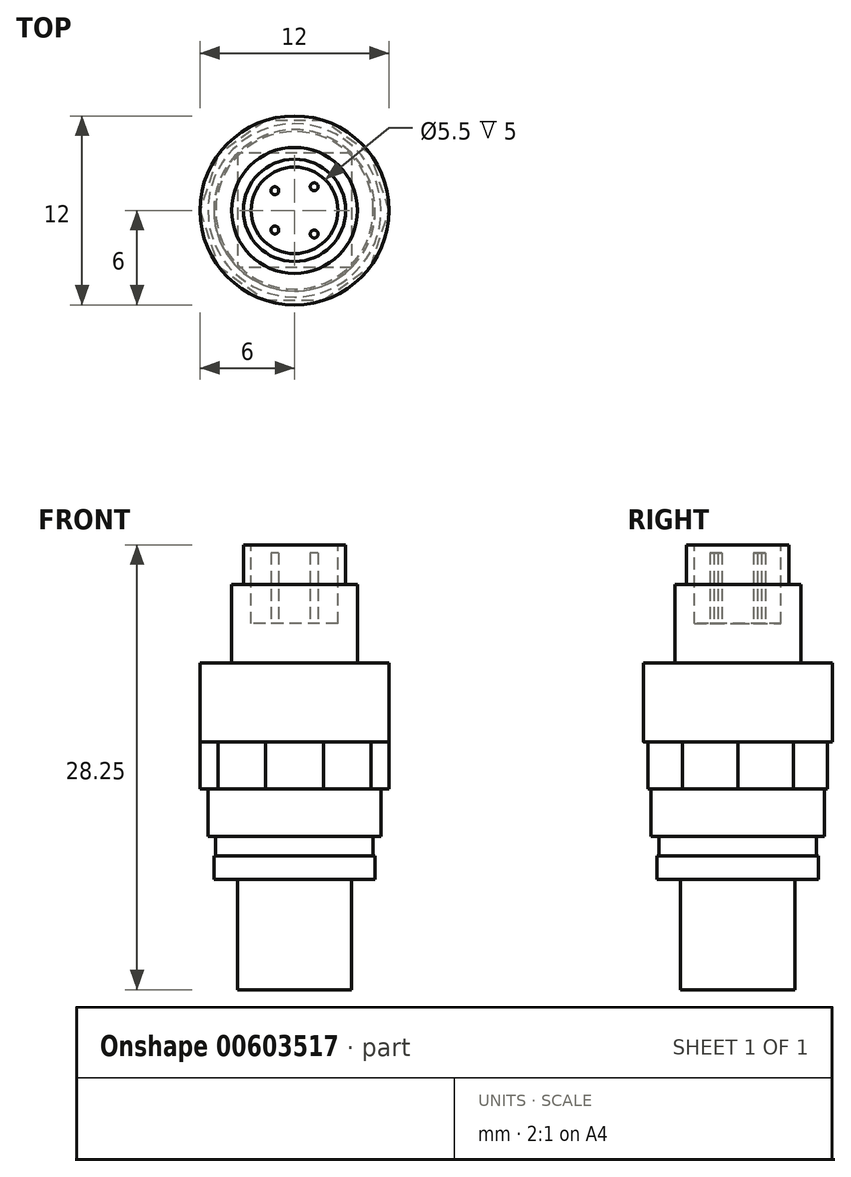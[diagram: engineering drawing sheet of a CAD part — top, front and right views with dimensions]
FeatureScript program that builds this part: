
annotation { "Feature Type Name" : "Feature", "Feature Type Description" : "" }
export const myFeature = defineFeature(function(context is Context, id is Id, definition is map)
    precondition{}
    {
        {
            var Q0;
            Q0=qCreatedBy(makeId("Top.planeOp"),FACE);
            var sketch = newSketch(context, id + "F0", { "sketchPlane" : qUnion([Q0])});
            skCircle(sketch, "E0", {"center": v(0, 0) * mm, "radius": 3.25 * mm});
            skSolve(sketch);
        }
        {
            var Q0;
            Q0=makeQuery(id+"F0.imprint","IMPRINT",FACE,{"disambiguationData":[TD([[makeQuery(id+"F0.imprint","IMPRINT",EDGE,{"derivedFrom":sQuery(id+"F0.wireOp",EDGE,"E0")}),1.0]])]});
            extrude(context, id + "F1", {"entities" : qUnion([Q0]), "oppositeDirection" : true, "depth" : 2.5 * mm, "offsetDistance" : 25 * mm});
        }
        {
            var Q0;
            Q0=makeQuery(id+"F1.opExtrude","CAP_FACE",FACE,{"disambiguationData":[OSD([sQuery(id+"F0.wireOp",EDGE,"E0")])],"isStart":false});
            var sketch = newSketch(context, id + "F2", { "sketchPlane" : qUnion([Q0])});
            skCircle(sketch, "E1", {"center": v(0, 0) * mm, "radius": 4 * mm});
            skSolve(sketch);
        }
        {
            var Q0;
            Q0=makeQuery(id+"F2.imprint","IMPRINT",FACE,{"disambiguationData":[TD([[makeQuery(id+"F2.imprint","IMPRINT",EDGE,{"derivedFrom":makeQuery(id+"F1.opExtrude","CAP_EDGE",EDGE,{"disambiguationData":[OSD([sQuery(id+"F0.wireOp",EDGE,"E0")])],"isStart":false})}),-1.0]])]});
            var Q1;
            Q1=makeQuery(id+"F2.imprint","IMPRINT",FACE,{"disambiguationData":[TD([[makeQuery(id+"F2.imprint","IMPRINT",EDGE,{"derivedFrom":sQuery(id+"F2.wireOp",EDGE,"E1")}),1.0]])]});
            extrude(context, id + "F3", {"entities" : qUnion([Q0, Q1]), "operationType" : NewBodyOperationType.ADD, "depth" : 5 * mm, "offsetDistance" : 25 * mm});
        }
        {
            var Q0;
            Q0=makeQuery(id+"F3.opExtrude","CAP_FACE",FACE,{"disambiguationData":[OSD([sQuery(id+"F2.wireOp",EDGE,"E1")])],"isStart":false});
            var sketch = newSketch(context, id + "F4", { "sketchPlane" : qUnion([Q0])});
            skCircle(sketch, "E2", {"center": v(0, 0) * mm, "radius": 6 * mm});
            skSolve(sketch);
        }
        {
            var Q0;
            Q0=makeQuery(id+"F4.imprint","IMPRINT",FACE,{"disambiguationData":[TD([[makeQuery(id+"F4.imprint","IMPRINT",EDGE,{"derivedFrom":sQuery(id+"F4.wireOp",EDGE,"E2")}),1.0]])]});
            var Q1;
            Q1=makeQuery(id+"F4.imprint","IMPRINT",FACE,{"disambiguationData":[TD([[makeQuery(id+"F4.imprint","IMPRINT",EDGE,{"derivedFrom":makeQuery(id+"F3.opExtrude","CAP_EDGE",EDGE,{"disambiguationData":[OSD([sQuery(id+"F2.wireOp",EDGE,"E1")])],"isStart":false})}),1.0]])]});
            extrude(context, id + "F5", {"entities" : qUnion([Q0, Q1]), "operationType" : NewBodyOperationType.ADD, "depth" : 5 * mm, "offsetDistance" : 25 * mm});
        }
        {
            var Q0;
            Q0=makeQuery(id+"F5.opExtrude","CAP_FACE",FACE,{"disambiguationData":[OSD([sQuery(id+"F4.wireOp",EDGE,"E2")])],"isStart":false});
            var sketch = newSketch(context, id + "F6", { "sketchPlane" : qUnion([Q0])});
            skCircle(sketch, "E3.cCircle", {"center": v(0, 0) * mm, "radius": 6 * mm, "construction": true});
            skLineSegment(sketch, "E3.0", {"start": v(6, 0) * mm, "end": v(4.85, -3.53) * mm});
            skLineSegment(sketch, "E3.1", {"start": v(4.85, -3.53) * mm, "end": v(1.85, -5.7) * mm});
            skLineSegment(sketch, "E3.2", {"start": v(1.85, -5.7) * mm, "end": v(-1.85, -5.7) * mm});
            skLineSegment(sketch, "E3.3", {"start": v(-1.85, -5.7) * mm, "end": v(-4.85, -3.53) * mm});
            skLineSegment(sketch, "E3.4", {"start": v(-4.85, -3.53) * mm, "end": v(-6, 0) * mm});
            skLineSegment(sketch, "E3.5", {"start": v(-6, 0) * mm, "end": v(-4.85, 3.53) * mm});
            skLineSegment(sketch, "E3.6", {"start": v(-4.85, 3.53) * mm, "end": v(-1.85, 5.7) * mm});
            skLineSegment(sketch, "E3.7", {"start": v(-1.85, 5.7) * mm, "end": v(1.85, 5.7) * mm});
            skLineSegment(sketch, "E3.8", {"start": v(1.85, 5.7) * mm, "end": v(4.85, 3.53) * mm});
            skLineSegment(sketch, "E3.9", {"start": v(4.85, 3.53) * mm, "end": v(6, 0) * mm});
            skSolve(sketch);
        }
        {
            var Q0;
            Q0=makeQuery(id+"F6.imprint","IMPRINT",FACE,{"disambiguationData":[TD([[makeQuery(id+"F6.imprint","IMPRINT",EDGE,{"derivedFrom":sQuery(id+"F6.wireOp",EDGE,"E3.0")}),-1.0]])]});
            extrude(context, id + "F7", {"entities" : qUnion([Q0]), "operationType" : NewBodyOperationType.ADD, "depth" : 3 * mm, "offsetDistance" : 25 * mm});
        }
        {
            var Q0;
            Q0=makeQuery(id+"F7.opExtrude","CAP_FACE",FACE,{"disambiguationData":[OSD([sQuery(id+"F6.wireOp",EDGE,"E3.0"),sQuery(id+"F6.wireOp",EDGE,"E3.1"),sQuery(id+"F6.wireOp",EDGE,"E3.2"),sQuery(id+"F6.wireOp",EDGE,"E3.3"),sQuery(id+"F6.wireOp",EDGE,"E3.4"),sQuery(id+"F6.wireOp",EDGE,"E3.5"),sQuery(id+"F6.wireOp",EDGE,"E3.6"),sQuery(id+"F6.wireOp",EDGE,"E3.7"),sQuery(id+"F6.wireOp",EDGE,"E3.8"),sQuery(id+"F6.wireOp",EDGE,"E3.9")])],"isStart":false});
            var sketch = newSketch(context, id + "F8", { "sketchPlane" : qUnion([Q0])});
            skCircle(sketch, "E4", {"center": v(0, 0) * mm, "radius": 5.5 * mm});
            skSolve(sketch);
        }
        {
            var Q0;
            Q0=makeQuery(id+"F8.imprint","IMPRINT",FACE,{"disambiguationData":[TD([[makeQuery(id+"F8.imprint","IMPRINT",EDGE,{"derivedFrom":sQuery(id+"F8.wireOp",EDGE,"E4")}),1.0]])]});
            extrude(context, id + "F9", {"entities" : qUnion([Q0]), "operationType" : NewBodyOperationType.ADD, "depth" : 3 * mm, "offsetDistance" : 25 * mm});
        }
        {
            var Q0;
            Q0=makeQuery(id+"F9.opExtrude","CAP_FACE",FACE,{"disambiguationData":[OSD([sQuery(id+"F8.wireOp",EDGE,"E4")])],"isStart":false});
            var sketch = newSketch(context, id + "F10", { "sketchPlane" : qUnion([Q0])});
            skCircle(sketch, "E5", {"center": v(0, 0) * mm, "radius": 5 * mm});
            skSolve(sketch);
        }
        {
            var Q0;
            Q0=makeQuery(id+"F10.imprint","IMPRINT",FACE,{"disambiguationData":[TD([[makeQuery(id+"F10.imprint","IMPRINT",EDGE,{"derivedFrom":sQuery(id+"F10.wireOp",EDGE,"E5")}),1.0]])]});
            extrude(context, id + "F11", {"entities" : qUnion([Q0]), "operationType" : NewBodyOperationType.ADD, "depth" : 1.25 * mm, "offsetDistance" : 25 * mm});
        }
        {
            var Q0;
            Q0=makeQuery(id+"F11.opExtrude","CAP_FACE",FACE,{"disambiguationData":[OSD([sQuery(id+"F10.wireOp",EDGE,"E5")])],"isStart":false});
            var sketch = newSketch(context, id + "F12", { "sketchPlane" : qUnion([Q0])});
            skCircle(sketch, "E6", {"center": v(0, 0) * mm, "radius": 5.13 * mm});
            skSolve(sketch);
        }
        {
            var Q0;
            Q0=makeQuery(id+"F12.imprint","IMPRINT",FACE,{"disambiguationData":[TD([[makeQuery(id+"F12.imprint","IMPRINT",EDGE,{"derivedFrom":sQuery(id+"F12.wireOp",EDGE,"E6")}),1.0]])]});
            var Q1;
            Q1=makeQuery(id+"F12.imprint","IMPRINT",FACE,{"disambiguationData":[TD([[makeQuery(id+"F12.imprint","IMPRINT",EDGE,{"derivedFrom":makeQuery(id+"F11.opExtrude","CAP_EDGE",EDGE,{"disambiguationData":[OSD([sQuery(id+"F10.wireOp",EDGE,"E5")])],"isStart":false})}),1.0]])]});
            extrude(context, id + "F13", {"entities" : qUnion([Q0, Q1]), "operationType" : NewBodyOperationType.ADD, "depth" : 1.5 * mm, "offsetDistance" : 25 * mm});
        }
        {
            var Q0;
            Q0=makeQuery(id+"F13.opExtrude","CAP_FACE",FACE,{"disambiguationData":[OSD([sQuery(id+"F12.wireOp",EDGE,"E6")])],"isStart":false});
            var sketch = newSketch(context, id + "F14", { "sketchPlane" : qUnion([Q0])});
            skLineSegment(sketch, "E7.bottom", {"start": v(3.62, -3.62) * mm, "end": v(-3.62, -3.62) * mm});
            skLineSegment(sketch, "E7.top", {"start": v(3.62, 3.62) * mm, "end": v(-3.62, 3.62) * mm});
            skLineSegment(sketch, "E7.left", {"start": v(3.62, -3.62) * mm, "end": v(3.62, 3.62) * mm});
            skLineSegment(sketch, "E7.right", {"start": v(-3.62, -3.62) * mm, "end": v(-3.62, 3.62) * mm});
            skPoint(sketch, "E7.middle", {"position": v(0, 0) * mm});
            skSolve(sketch);
        }
        {
            var Q0;
            Q0=makeQuery(id+"F14.imprint","IMPRINT",FACE,{"disambiguationData":[TD([[makeQuery(id+"F14.imprint","IMPRINT",EDGE,{"derivedFrom":sQuery(id+"F14.wireOp",EDGE,"E7.bottom")}),-1.0]])]});
            extrude(context, id + "F15", {"entities" : qUnion([Q0]), "operationType" : NewBodyOperationType.ADD, "depth" : 7 * mm, "offsetDistance" : 25 * mm});
        }
        {
            var Q0;
            Q0=makeQuery(id+"F1.opExtrude","CAP_FACE",FACE,{"disambiguationData":[OSD([sQuery(id+"F0.wireOp",EDGE,"E0")])],"isStart":true});
            var sketch = newSketch(context, id + "F16", { "sketchPlane" : qUnion([Q0])});
            skCircle(sketch, "E8.0", {"center": v(0, 0) * mm, "radius": 3.25 * mm, "construction": true});
            skCircle(sketch, "E9.0", {"center": v(0, 0) * mm, "radius": 2.75 * mm});
            skSolve(sketch);
        }
        {
            var Q0;
            Q0=makeQuery(id+"F16.imprint","IMPRINT",FACE,{"disambiguationData":[TD([[makeQuery(id+"F16.imprint","IMPRINT",EDGE,{"derivedFrom":sQuery(id+"F16.wireOp",EDGE,"E9.0")}),1.0]])]});
            extrude(context, id + "F17", {"entities" : qUnion([Q0]), "operationType" : NewBodyOperationType.REMOVE, "oppositeDirection" : true, "depth" : 5 * mm, "offsetDistance" : 25 * mm});
        }
        {
            var Q0;
            Q0=makeQuery(id+"F17.boolean.opBoolean","COPY",FACE,{"derivedFrom":makeQuery(id+"F17.opExtrude","CAP_FACE",FACE,{"disambiguationData":[OSD([sQuery(id+"F16.wireOp",EDGE,"E9.0")])],"isStart":false})});
            var sketch = newSketch(context, id + "F18", { "sketchPlane" : qUnion([Q0])});
            skCircle(sketch, "E10", {"center": v(-1.25, -1.25) * mm, "radius": 0.25 * mm});
            skCircle(sketch, "E11", {"center": v(-1.25, 1.25) * mm, "radius": 0.25 * mm});
            skCircle(sketch, "E12", {"center": v(1.25, -1.5) * mm, "radius": 0.25 * mm});
            skCircle(sketch, "E13", {"center": v(1.25, 1.5) * mm, "radius": 0.25 * mm});
            skLineSegment(sketch, "E14.bottom", {"start": v(1.25, 1.25) * mm, "end": v(-1.25, 1.25) * mm, "construction": true});
            skLineSegment(sketch, "E14.top", {"start": v(1.25, -1.25) * mm, "end": v(-1.25, -1.25) * mm, "construction": true});
            skLineSegment(sketch, "E14.left", {"start": v(1.25, 1.25) * mm, "end": v(1.25, -1.25) * mm, "construction": true});
            skLineSegment(sketch, "E14.right", {"start": v(-1.25, 1.25) * mm, "end": v(-1.25, -1.25) * mm, "construction": true});
            skPoint(sketch, "E14.middle", {"position": v(0, 0) * mm});
            skSolve(sketch);
        }
        {
            var Q0;
            Q0=makeQuery(id+"F18.imprint","IMPRINT",FACE,{"disambiguationData":[TD([[makeQuery(id+"F18.imprint","IMPRINT",EDGE,{"derivedFrom":sQuery(id+"F18.wireOp",EDGE,"E10")}),1.0]])]});
            var Q1;
            Q1=makeQuery(id+"F18.imprint","IMPRINT",FACE,{"disambiguationData":[TD([[makeQuery(id+"F18.imprint","IMPRINT",EDGE,{"derivedFrom":sQuery(id+"F18.wireOp",EDGE,"E12")}),1.0]])]});
            var Q2;
            Q2=makeQuery(id+"F18.imprint","IMPRINT",FACE,{"disambiguationData":[TD([[makeQuery(id+"F18.imprint","IMPRINT",EDGE,{"derivedFrom":sQuery(id+"F18.wireOp",EDGE,"E13")}),1.0]])]});
            var Q3;
            Q3=makeQuery(id+"F18.imprint","IMPRINT",FACE,{"disambiguationData":[TD([[makeQuery(id+"F18.imprint","IMPRINT",EDGE,{"derivedFrom":sQuery(id+"F18.wireOp",EDGE,"E11")}),1.0]])]});
            extrude(context, id + "F19", {"entities" : qUnion([Q0, Q1, Q2, Q3]), "operationType" : NewBodyOperationType.ADD, "depth" : 4.5 * mm, "offsetDistance" : 25 * mm});
        }
    });
